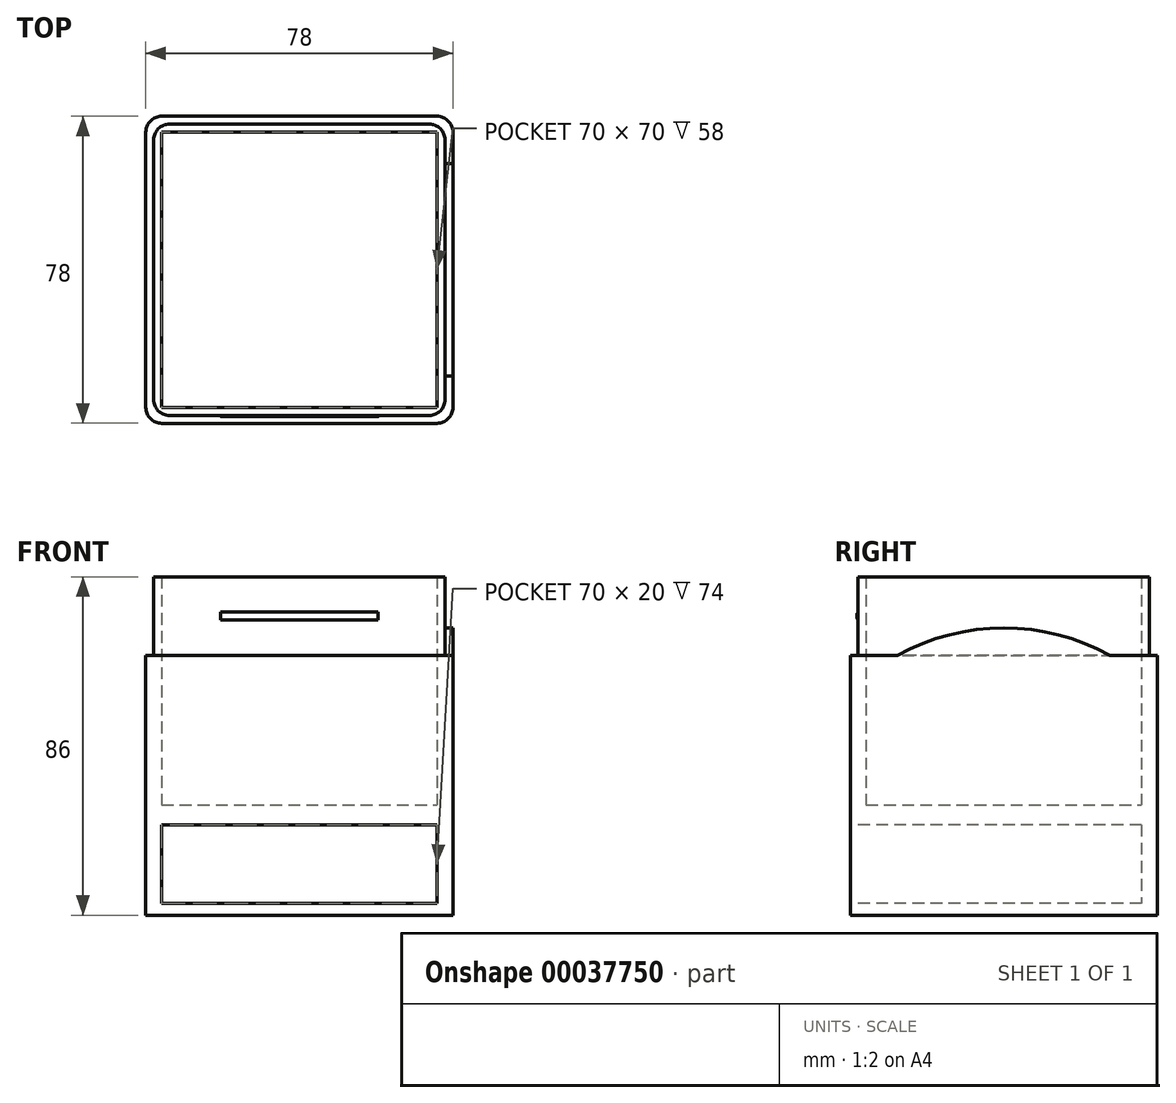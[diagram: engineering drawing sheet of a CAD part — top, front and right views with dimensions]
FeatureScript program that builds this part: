
annotation { "Feature Type Name" : "Feature", "Feature Type Description" : "" }
export const myFeature = defineFeature(function(context is Context, id is Id, definition is map)
    precondition{}
    {
        {
            var Q0;
            Q0=qCreatedBy(makeId("Top.planeOp"),FACE);
            var sketch = newSketch(context, id + "F0", { "sketchPlane" : qUnion([Q0])});
            skLineSegment(sketch, "E0.bottom", {"start": v(-77.74, -18.91) * mm, "end": v(0.26, -18.91) * mm});
            skLineSegment(sketch, "E0.top", {"start": v(-77.74, 59.09) * mm, "end": v(0.26, 59.09) * mm});
            skLineSegment(sketch, "E0.left", {"start": v(-77.74, -18.91) * mm, "end": v(-77.74, 59.09) * mm});
            skLineSegment(sketch, "E0.right", {"start": v(0.26, -18.91) * mm, "end": v(0.26, 59.09) * mm});
            skSolve(sketch);
        }
        {
            var Q0;
            Q0 = qSketchRegion(id + "F0", true);
            extrude(context, id + "F1", {"entities" : qUnion([Q0]), "depth" : 86 * mm});
        }
        {
            var Q0;
            Q0=makeQuery(id+"F1.opExtrude","CAP_FACE",FACE,{"disambiguationData":[OSD([sQuery(id+"F0.wireOp",EDGE,"E0.bottom"),sQuery(id+"F0.wireOp",EDGE,"E0.top"),sQuery(id+"F0.wireOp",EDGE,"E0.left"),sQuery(id+"F0.wireOp",EDGE,"E0.right")])],"isStart":false});
            shell(context, id + "F2", {"entities" : qUnion([Q0]), "thickness" : 4 * mm});
        }
        {
            var Q0;
            Q0=makeQuery(id+"F1.opExtrude","SWEPT_FACE",FACE,{"disambiguationData":[OSD([sQuery(id+"F0.wireOp",EDGE,"E0.bottom")])]});
            var sketch = newSketch(context, id + "F3", { "sketchPlane" : qUnion([Q0])});
            skLineSegment(sketch, "E1.bottom", {"start": v(-73.74, 23) * mm, "end": v(-3.74, 23) * mm});
            skLineSegment(sketch, "E1.top", {"start": v(-73.74, 3) * mm, "end": v(-3.74, 3) * mm});
            skLineSegment(sketch, "E1.left", {"start": v(-73.74, 23) * mm, "end": v(-73.74, 3) * mm});
            skLineSegment(sketch, "E1.right", {"start": v(-3.74, 23) * mm, "end": v(-3.74, 3) * mm});
            skLineSegment(sketch, "E2.0", {"start": v(-77.74, 86) * mm, "end": v(-77.74, 0) * mm});
            skLineSegment(sketch, "E3.0", {"start": v(0.26, 86) * mm, "end": v(0.26, 0) * mm});
            skLineSegment(sketch, "E4.0", {"start": v(-77.74, 0) * mm, "end": v(0.26, 0) * mm});
            skSolve(sketch);
        }
        {
            var Q0;
            Q0=makeQuery(id+"F2.opShell","OFFSET_FACE",FACE,{"disambiguationData":[OSD([sQuery(id+"F0.wireOp",EDGE,"E0.bottom"),sQuery(id+"F0.wireOp",EDGE,"E0.top"),sQuery(id+"F0.wireOp",EDGE,"E0.left"),sQuery(id+"F0.wireOp",EDGE,"E0.right")])]});
            extrude(context, id + "F4", {"entities" : qUnion([Q0]), "operationType" : NewBodyOperationType.ADD, "depth" : 24 * mm});
        }
        {
            var Q0;
            Q0 = qSketchRegion(id + "F3", true);
            extrude(context, id + "F5", {"entities" : qUnion([Q0]), "operationType" : NewBodyOperationType.REMOVE, "oppositeDirection" : true, "depth" : 74 * mm});
        }
        {
            var Q0;
            Q0=makeQuery(id+"F1.opExtrude","CAP_FACE",FACE,{"disambiguationData":[OSD([sQuery(id+"F0.wireOp",EDGE,"E0.bottom"),sQuery(id+"F0.wireOp",EDGE,"E0.top"),sQuery(id+"F0.wireOp",EDGE,"E0.left"),sQuery(id+"F0.wireOp",EDGE,"E0.right")])],"isStart":false});
            var sketch = newSketch(context, id + "F6", { "sketchPlane" : qUnion([Q0])});
            skLineSegment(sketch, "E5", {"start": v(-77.74, 59.09) * mm, "end": v(0.26, -18.91) * mm, "construction": true});
            skLineSegment(sketch, "E6", {"start": v(-77.74, -18.91) * mm, "end": v(0.26, 59.09) * mm, "construction": true});
            skLineSegment(sketch, "E7.rect.bottom", {"start": v(-75.74, 57.09) * mm, "end": v(-1.74, 57.09) * mm});
            skLineSegment(sketch, "E7.rect.top", {"start": v(-75.74, -16.91) * mm, "end": v(-1.74, -16.91) * mm});
            skLineSegment(sketch, "E7.rect.left", {"start": v(-75.74, 57.09) * mm, "end": v(-75.74, -16.91) * mm});
            skLineSegment(sketch, "E7.rect.right", {"start": v(-1.74, 57.09) * mm, "end": v(-1.74, -16.91) * mm});
            skPoint(sketch, "E7.rect.middle", {"position": v(-38.74, 20.09) * mm});
            skSolve(sketch);
        }
        {
            var Q0;
            Q0=makeQuery(id+"F6.imprint","IMPRINT",FACE,{"disambiguationData":[TD([[makeQuery(id+"F6.imprint","IMPRINT",EDGE,{"derivedFrom":sQuery(id+"F6.wireOp",EDGE,"E7.rect.bottom")}),1.0]])]});
            extrude(context, id + "F7", {"entities" : qUnion([Q0]), "operationType" : NewBodyOperationType.REMOVE, "oppositeDirection" : true, "depth" : 20 * mm});
        }
        {
            var Q0;
            Q0=makeQuery(id+"F7.boolean.opBoolean","COPY",FACE,{"derivedFrom":makeQuery(id+"F7.opExtrude","SWEPT_FACE",FACE,{"disambiguationData":[OSD([sQuery(id+"F6.wireOp",EDGE,"E7.rect.right")])]})});
            var sketch = newSketch(context, id + "F8", { "sketchPlane" : qUnion([Q0])});
            skArc(sketch, "E8", {"start": v(47.09, 66) * mm, "mid": v(20.09, 73) * mm, "end": v(-6.91, 66) * mm});
            skLineSegment(sketch, "E9", {"start": v(20.09, 73) * mm, "end": v(20.09, 66) * mm, "construction": true});
            skSolve(sketch);
        }
        {
            var Q0;
            {var subQ1=sQuery(id+"F8.wireOp",EDGE,"E8");Q0=makeQuery(id+"F8.imprint","IMPRINT",FACE,{"disambiguationData":[TD([[makeQuery(id+"F8.imprint","IMPRINT",EDGE,{"derivedFrom":subQ1}),1.0]])]});}
            extrude(context, id + "F9", {"entities" : qUnion([Q0]), "operationType" : NewBodyOperationType.ADD, "depth" : 2 * mm});
        }
        {
            var Q0;
            Q0=makeQuery(id+"F1.opExtrude","SWEPT_EDGE",EDGE,{"disambiguationData":[OSD([sQuery(id+"F0.wireOp",EDGE,"E0.bottom"),sQuery(id+"F0.wireOp",EDGE,"E0.left")])]});
            var Q1;
            Q1=makeQuery(id+"F1.opExtrude","SWEPT_EDGE",EDGE,{"disambiguationData":[OSD([sQuery(id+"F0.wireOp",EDGE,"E0.bottom"),sQuery(id+"F0.wireOp",EDGE,"E0.right")])]});
            var Q2;
            Q2=makeQuery(id+"F1.opExtrude","SWEPT_EDGE",EDGE,{"disambiguationData":[OSD([sQuery(id+"F0.wireOp",EDGE,"E0.top"),sQuery(id+"F0.wireOp",EDGE,"E0.right")])]});
            var Q3;
            Q3=makeQuery(id+"F1.opExtrude","SWEPT_EDGE",EDGE,{"disambiguationData":[OSD([sQuery(id+"F0.wireOp",EDGE,"E0.top"),sQuery(id+"F0.wireOp",EDGE,"E0.left")])]});
            fillet(context, id + "F10", {"entities" : qUnion([Q0, Q1, Q2, Q3]), "radius" : 4 * mm, "tangentPropagation" : true, "allowEdgeOverflow" : false});
        }
        {
            var Q0;
            Q0=makeQuery(id+"F7.boolean.opBoolean","COPY",EDGE,{"derivedFrom":makeQuery(id+"F7.opExtrude","SWEPT_EDGE",EDGE,{"disambiguationData":[OSD([sQuery(id+"F6.wireOp",EDGE,"E7.rect.top"),sQuery(id+"F6.wireOp",EDGE,"E7.rect.right")])]})});
            var Q1;
            Q1=makeQuery(id+"F7.boolean.opBoolean","COPY",EDGE,{"derivedFrom":makeQuery(id+"F7.opExtrude","SWEPT_EDGE",EDGE,{"disambiguationData":[OSD([sQuery(id+"F6.wireOp",EDGE,"E7.rect.bottom"),sQuery(id+"F6.wireOp",EDGE,"E7.rect.right")])]})});
            var Q2;
            Q2=makeQuery(id+"F7.boolean.opBoolean","COPY",EDGE,{"derivedFrom":makeQuery(id+"F7.opExtrude","SWEPT_EDGE",EDGE,{"disambiguationData":[OSD([sQuery(id+"F6.wireOp",EDGE,"E7.rect.top"),sQuery(id+"F6.wireOp",EDGE,"E7.rect.left")])]})});
            var Q3;
            Q3=makeQuery(id+"F7.boolean.opBoolean","COPY",EDGE,{"derivedFrom":makeQuery(id+"F7.opExtrude","SWEPT_EDGE",EDGE,{"disambiguationData":[OSD([sQuery(id+"F6.wireOp",EDGE,"E7.rect.bottom"),sQuery(id+"F6.wireOp",EDGE,"E7.rect.left")])]})});
            fillet(context, id + "F11", {"entities" : qUnion([Q0, Q1, Q2, Q3]), "radius" : 4 * mm, "tangentPropagation" : true, "allowEdgeOverflow" : false});
        }
        {
            var Q0;
            Q0=makeQuery(id+"F7.boolean.opBoolean","COPY",FACE,{"derivedFrom":makeQuery(id+"F7.opExtrude","SWEPT_FACE",FACE,{"disambiguationData":[OSD([sQuery(id+"F6.wireOp",EDGE,"E7.rect.top")])]})});
            var sketch = newSketch(context, id + "F12", { "sketchPlane" : qUnion([Q0])});
            skLineSegment(sketch, "E10", {"start": v(-71.74, 86) * mm, "end": v(-5.74, 66) * mm, "construction": true});
            skLineSegment(sketch, "E11", {"start": v(-71.74, 66) * mm, "end": v(-5.74, 86) * mm, "construction": true});
            skLineSegment(sketch, "E12", {"start": v(-71.74, 76) * mm, "end": v(-5.74, 76) * mm, "construction": true});
            skLineSegment(sketch, "E13", {"start": v(-58.74, 75) * mm, "end": v(-18.74, 75) * mm});
            skLineSegment(sketch, "E14.MirrorCS", {"start": v(-58.74, 77) * mm, "end": v(-18.74, 77) * mm});
            skLineSegment(sketch, "E15", {"start": v(-58.74, 77) * mm, "end": v(-58.74, 75) * mm});
            skLineSegment(sketch, "E16", {"start": v(-18.74, 77) * mm, "end": v(-18.74, 75) * mm});
            skSolve(sketch);
        }
        {
            var Q0;
            Q0=makeQuery(id+"F12.imprint","IMPRINT",FACE,{"disambiguationData":[TD([[makeQuery(id+"F12.imprint","IMPRINT",EDGE,{"derivedFrom":sQuery(id+"F12.wireOp",EDGE,"E13")}),1.0]])]});
            extrude(context, id + "F13", {"entities" : qUnion([Q0]), "operationType" : NewBodyOperationType.ADD, "depth" : 0.3 * mm});
        }
        {
            var Q0;
            Q0=makeQuery(id+"F13.opExtrude","CAP_EDGE",EDGE,{"disambiguationData":[OSD([sQuery(id+"F12.wireOp",EDGE,"E14.MirrorCS")])],"isStart":false});
            fillet(context, id + "F14", {"entities" : qUnion([Q0]), "radius" : 1 * mm, "tangentPropagation" : true, "allowEdgeOverflow" : false});
        }
        {
            var Q0;
            Q0=makeQuery(id+"F13.opExtrude","CAP_EDGE",EDGE,{"disambiguationData":[OSD([sQuery(id+"F12.wireOp",EDGE,"E13")])],"isStart":false});
            fillet(context, id + "F15", {"entities" : qUnion([Q0]), "radius" : 1 * mm, "tangentPropagation" : true, "allowEdgeOverflow" : false});
        }
    });
